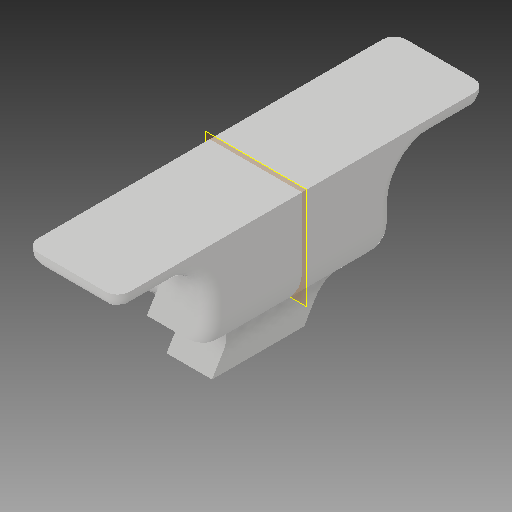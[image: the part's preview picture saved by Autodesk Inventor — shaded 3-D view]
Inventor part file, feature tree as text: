
AUTODESK INVENTOR PART (.ipt)
format: ipt  version: 2018 (Build 220112000, 112)  size: 267,264 bytes
history: native  units: in
note: dims shown in document units (in); Inventor stores cm internally (conversion verified against a paired STEP export)
features: extrude x10, sketch x9, fillet x5, plane x3, other x2, projected_geometry x1, reference x1
ambient origin geometry x8: Origin, YZ Plane, XZ Plane, XY Plane, X Axis, Y Axis, Z Axis, Center Point
bodies: Solid1 (feature_tree)
feature tree (31):
  extrude  "Extrusion1"  Depth=0.6in
  plane  "Work Plane1"
  plane  "Work Plane2"
  plane  "Work Plane3"
  extrude  "Extrusion4"  Depth=0.3in TaperAngle=0.0deg
  extrude  "Extrusion5"  Depth=1.0in TaperAngle=0.0deg
  extrude  "Extrusion7"  Depth=0.3in
  extrude  "Extrusion8"  Depth=0.3in
  extrude  "Extrusion9"  Depth=0.125in
  fillet  "Fillet3"  Radius=0.125in
  fillet  "Fillet4"  Radius=1000.0in
  extrude  "Extrusion11"  Depth=12.0in TaperAngle=0.0deg
  extrude  "Extrusion12"  Depth=0.0394in
  extrude  "Extrusion13"  Depth=0.0394in TaperAngle=0.0deg
  fillet  "Fillet6"  [1 undecoded]
  fillet  "Fillet7"  [1 undecoded]
  fillet  "Fillet8"  [1 undecoded]
  extrude  "Extrusion14"  [1 undecoded]
  sketch  "Sketch1"  dims[d0=0.3in d1=0.6in]
  sketch  "Sketch3"  dims[d2=0.3in d3=0.0in d8=0.3in d9=0.0in]
  sketch  "Sketch4"  dims[d10=1.0in d11=0.0in d14=1.0in d15=0.0in]
  sketch  "Sketch7"  dims[d16=1.0in d17=0.0in d18=0.3in]
  sketch  "Sketch8"  dims[d19=0.3in d20=0.3in]
  sketch  "Sketch10"  dims[d21=0.05in d22=0.0in d27=0.125in d28=0.125in d29=1000.0in d30=0.0in]
  sketch  "Sketch11"  dims[d31=1000.0in d32=0.0in d34=12.0in d35=0.0in]
  sketch  "Sketch12"  dims[d36=0.0394in d37=0.0394in]
  projected_geometry  "Projected Loop1"
  sketch  "Sketch13"  dims[d38=0.0394in d39=1.0in d40=0.5in d41=0.0in d42=0.0in]
  reference  "Reference1"
  other  "ArmTruss.iam"
  other  "straightBar:1"
note: 4 required parameter values undecoded (feature->parameter linkage not recoverable at this tier; creation-order binding heuristic only, values carry confidence <= 0.55)
